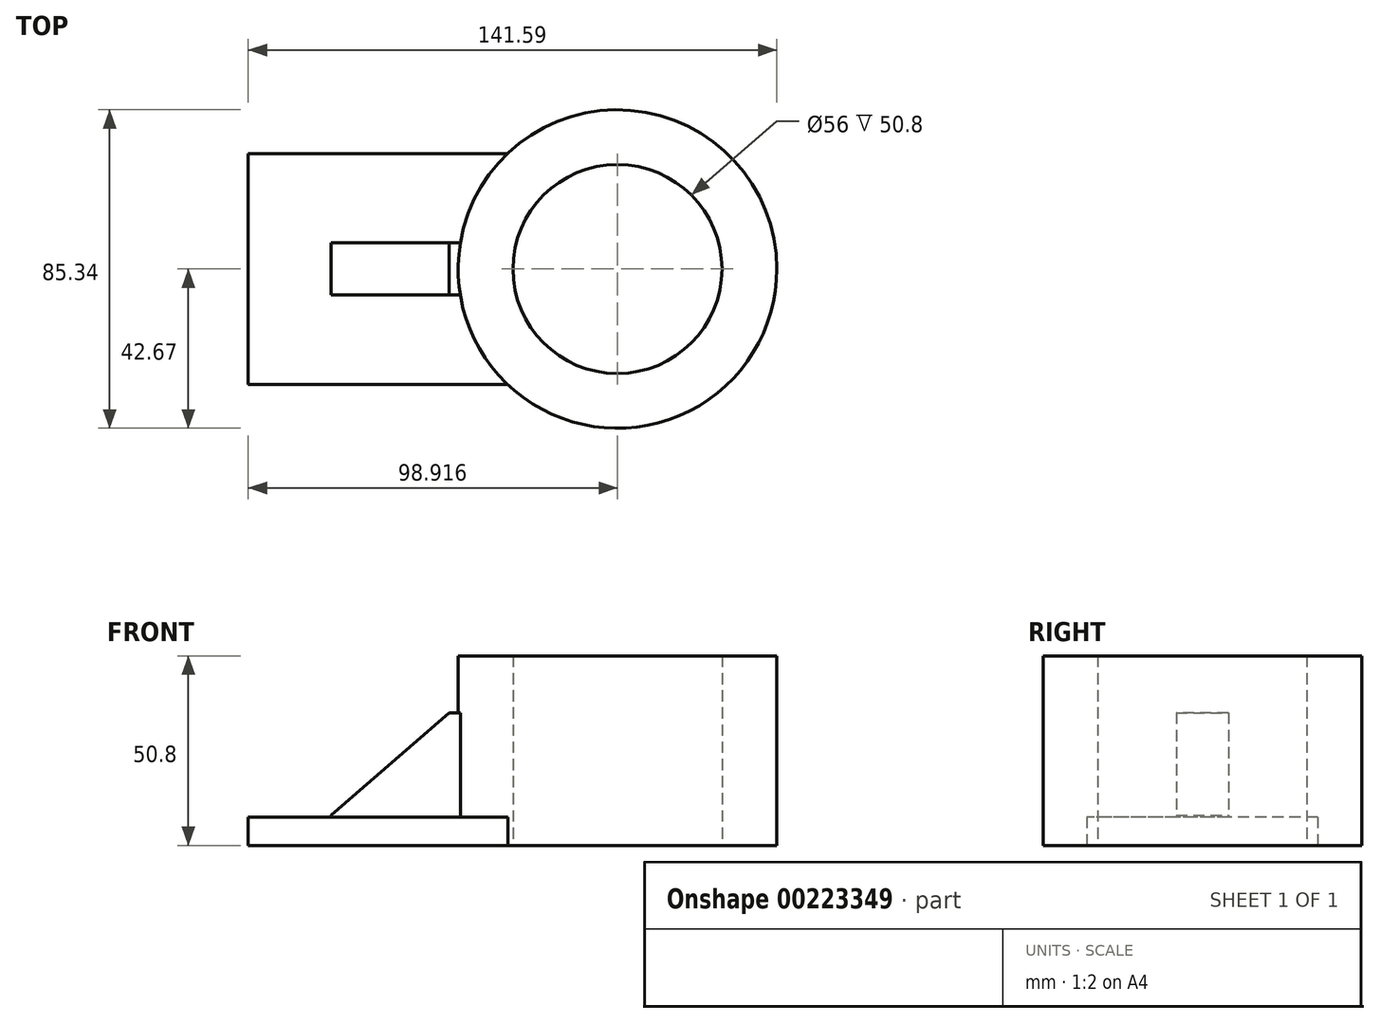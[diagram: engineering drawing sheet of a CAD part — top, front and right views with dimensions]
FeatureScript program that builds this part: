
annotation { "Feature Type Name" : "Feature", "Feature Type Description" : "" }
export const myFeature = defineFeature(function(context is Context, id is Id, definition is map)
    precondition{}
    {
        {
            var Q0;
            Q0=qCreatedBy(makeId("Top.planeOp"),FACE);
            var sketch = newSketch(context, id + "F0", { "sketchPlane" : qUnion([Q0])});
            skCircle(sketch, "E0", {"center": v(42.79, 0) * mm, "radius": 42.67 * mm});
            skCircle(sketch, "E1", {"center": v(42.79, 0) * mm, "radius": 28 * mm});
            skSolve(sketch);
        }
        {
            var Q0;
            Q0 = qSketchRegion(id + "F0", true);
            extrude(context, id + "F1", {"entities" : qUnion([Q0]), "depth" : 50.8 * mm});
        }
        {
            var Q0;
            Q0=qCreatedBy(makeId("Top.planeOp"),FACE);
            var sketch = newSketch(context, id + "F2", { "sketchPlane" : qUnion([Q0])});
            skLineSegment(sketch, "E2.bottom", {"start": v(-56.13, 30.95) * mm, "end": v(14.61, 30.95) * mm});
            skLineSegment(sketch, "E2.top", {"start": v(-56.13, -30.95) * mm, "end": v(14.61, -30.95) * mm});
            skLineSegment(sketch, "E2.left", {"start": v(-56.13, 30.95) * mm, "end": v(-56.13, -30.95) * mm});
            skLineSegment(sketch, "E2.right", {"start": v(14.61, 30.95) * mm, "end": v(14.61, -30.95) * mm});
            skPoint(sketch, "E2.middle", {"position": v(-20.76, 0) * mm});
            skSolve(sketch);
        }
        {
            var Q0;
            Q0 = qSketchRegion(id + "F2", true);
            extrude(context, id + "F3", {"entities" : qUnion([Q0]), "operationType" : NewBodyOperationType.ADD, "depth" : 7.62 * mm});
        }
        {
            var Q0;
            Q0=makeQuery(id+"F3.opExtrude","CAP_FACE",FACE,{"disambiguationData":[OSD([sQuery(id+"F2.wireOp",EDGE,"E2.bottom"),sQuery(id+"F2.wireOp",EDGE,"E2.top"),sQuery(id+"F2.wireOp",EDGE,"E2.left"),sQuery(id+"F2.wireOp",EDGE,"E2.right")])],"isStart":false});
            var sketch = newSketch(context, id + "F4", { "sketchPlane" : qUnion([Q0])});
            skLineSegment(sketch, "E3.bottom", {"start": v(-33.88, 6.99) * mm, "end": v(13.47, 6.99) * mm});
            skLineSegment(sketch, "E3.top", {"start": v(-33.88, -6.99) * mm, "end": v(13.47, -6.99) * mm});
            skLineSegment(sketch, "E3.left", {"start": v(-33.88, 6.99) * mm, "end": v(-33.88, -6.99) * mm});
            skLineSegment(sketch, "E3.right", {"start": v(13.47, 6.99) * mm, "end": v(13.47, -6.99) * mm});
            skPoint(sketch, "E3.middle", {"position": v(-10.2, 0) * mm});
            skSolve(sketch);
        }
        {
            var Q0;
            Q0 = qSketchRegion(id + "F4", true);
            extrude(context, id + "F5", {"entities" : qUnion([Q0]), "operationType" : NewBodyOperationType.ADD, "depth" : 27.94 * mm});
        }
        {
            var Q0;
            Q0=qCreatedBy(makeId("Front.planeOp"),FACE);
            var sketch = newSketch(context, id + "F6", { "sketchPlane" : qUnion([Q0])});
            skLineSegment(sketch, "E4", {"start": v(-34.16, 7.84) * mm, "end": v(0, 37.5) * mm});
            skLineSegment(sketch, "E5", {"start": v(0, 37.5) * mm, "end": v(-34.16, 37.5) * mm});
            skLineSegment(sketch, "E6", {"start": v(-34.16, 37.5) * mm, "end": v(-34.16, 7.84) * mm});
            skSolve(sketch);
        }
        {
            var Q0;
            Q0 = qSketchRegion(id + "F6", true);
            extrude(context, id + "F7", {"entities" : qUnion([Q0]), "operationType" : NewBodyOperationType.REMOVE, "oppositeDirection" : true, "depth" : 25.4 * mm, "hasSecondDirection" : true, "secondDirectionOppositeDirection" : false, "secondDirectionDepth" : 25.4 * mm});
        }
    });
